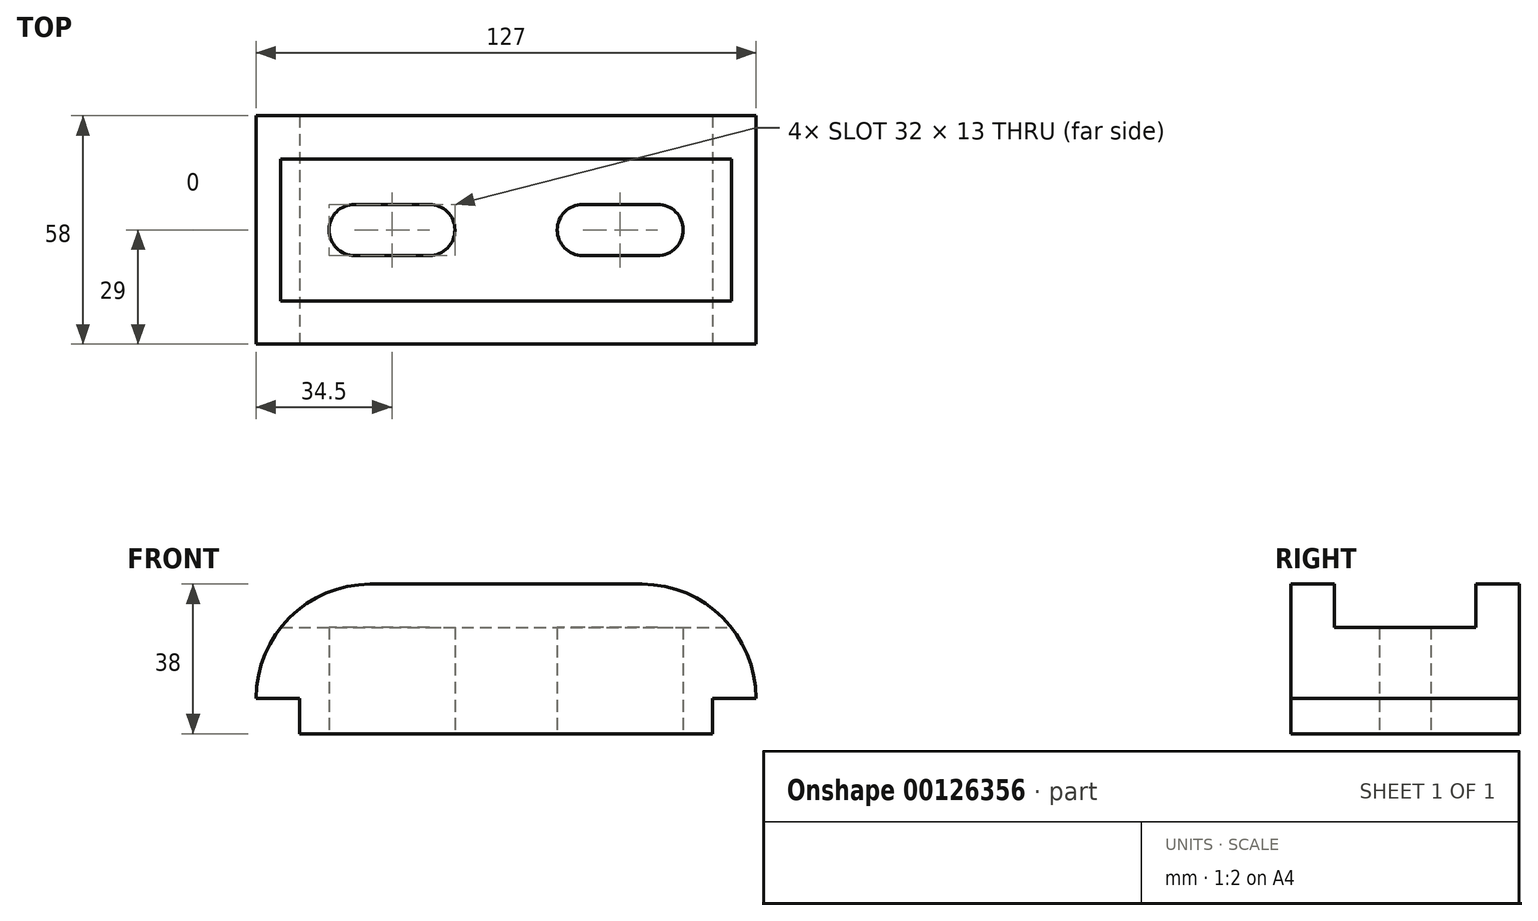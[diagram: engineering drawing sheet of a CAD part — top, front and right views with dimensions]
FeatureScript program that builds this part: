
annotation { "Feature Type Name" : "Feature", "Feature Type Description" : "" }
export const myFeature = defineFeature(function(context is Context, id is Id, definition is map)
    precondition{}
    {
        {
            var Q0;
            Q0=qCreatedBy(makeId("Front.planeOp"),FACE);
            var sketch = newSketch(context, id + "F0", { "sketchPlane" : qUnion([Q0])});
            skLineSegment(sketch, "E0", {"start": v(0, 0) * mm, "end": v(0, 9) * mm});
            skLineSegment(sketch, "E1", {"start": v(0, 9) * mm, "end": v(-11, 9) * mm});
            skLineSegment(sketch, "E2", {"start": v(-11, 9) * mm, "end": v(-11, 38) * mm});
            skLineSegment(sketch, "E3", {"start": v(0, 0) * mm, "end": v(105, 0) * mm});
            skLineSegment(sketch, "E4", {"start": v(105, 0) * mm, "end": v(105, 9) * mm});
            skLineSegment(sketch, "E5", {"start": v(105, 9) * mm, "end": v(116, 9) * mm});
            skLineSegment(sketch, "E6", {"start": v(116, 9) * mm, "end": v(116, 38) * mm});
            skLineSegment(sketch, "E7", {"start": v(116, 38) * mm, "end": v(-11, 38) * mm});
            skArc(sketch, "E8", {"start": v(18, 38) * mm, "mid": v(-2.5, 29.5) * mm, "end": v(-11, 9) * mm});
            skArc(sketch, "E9", {"start": v(116, 9) * mm, "mid": v(107.5, 29.5) * mm, "end": v(87, 38) * mm});
            skSolve(sketch);
        }
        {
            var Q0;
            Q0=makeQuery(id+"F0.imprint","IMPRINT",FACE,{"disambiguationData":[TD([[makeQuery(id+"F0.imprint","IMPRINT",EDGE,{"derivedFrom":sQuery(id+"F0.wireOp",EDGE,"E0")}),-1.0]])]});
            extrude(context, id + "F1", {"entities" : qUnion([Q0]), "oppositeDirection" : true, "depth" : 58 * mm});
        }
        {
            var Q0;
            Q0=qCreatedBy(makeId("Right.planeOp"),FACE);
            var sketch = newSketch(context, id + "F2", { "sketchPlane" : qUnion([Q0])});
            skLineSegment(sketch, "E10", {"start": v(0, 0) * mm, "end": v(11, 0) * mm, "construction": true});
            skLineSegment(sketch, "E11", {"start": v(11, 0) * mm, "end": v(47, 0) * mm, "construction": true});
            skLineSegment(sketch, "E12", {"start": v(11, 0) * mm, "end": v(11, 27) * mm, "construction": true});
            skLineSegment(sketch, "E13", {"start": v(11, 27) * mm, "end": v(11, 38) * mm});
            skLineSegment(sketch, "E14", {"start": v(11, 38) * mm, "end": v(47, 38) * mm});
            skLineSegment(sketch, "E15", {"start": v(47, 38) * mm, "end": v(47, 27) * mm});
            skLineSegment(sketch, "E16", {"start": v(47, 27) * mm, "end": v(11, 27) * mm});
            skSolve(sketch);
        }
        {
            var Q0;
            Q0 = qSketchRegion(id + "F2", true);
            extrude(context, id + "F3", {"entities" : qUnion([Q0]), "operationType" : NewBodyOperationType.REMOVE, "endBound" : BoundingType.SYMMETRIC, "oppositeDirection" : true, "depth" : 300 * mm});
        }
        {
            var Q0;
            Q0=makeQuery(id+"F1.opExtrude","SWEPT_FACE",FACE,{"disambiguationData":[OSD([sQuery(id+"F0.wireOp",EDGE,"E3")])]});
            var sketch = newSketch(context, id + "F4", { "sketchPlane" : qUnion([Q0])});
            skLineSegment(sketch, "E17", {"start": v(0, 0) * mm, "end": v(0, -29) * mm, "construction": true});
            skLineSegment(sketch, "E18", {"start": v(0, -29) * mm, "end": v(14, -29) * mm, "construction": true});
            skLineSegment(sketch, "E19", {"start": v(14, -29) * mm, "end": v(33, -29) * mm, "construction": true});
            skLineSegment(sketch, "E20", {"start": v(105, -29) * mm, "end": v(91, -29) * mm, "construction": true});
            skPoint(sketch, "E20.endSnap0", {"position": v(105, -29) * mm});
            skLineSegment(sketch, "E21", {"start": v(91, -29) * mm, "end": v(72, -29) * mm, "construction": true});
            skArc(sketch, "E22", {"start": v(14, -22.5) * mm, "mid": v(7.5, -29) * mm, "end": v(14, -35.5) * mm});
            skArc(sketch, "E23", {"start": v(33, -35.5) * mm, "mid": v(39.5, -29) * mm, "end": v(33, -22.5) * mm});
            skArc(sketch, "E24", {"start": v(72, -22.5) * mm, "mid": v(65.5, -29) * mm, "end": v(72, -35.5) * mm});
            skArc(sketch, "E25", {"start": v(91, -35.5) * mm, "mid": v(97.5, -29) * mm, "end": v(91, -22.5) * mm});
            skLineSegment(sketch, "E26", {"start": v(14, -22.5) * mm, "end": v(33, -22.5) * mm});
            skLineSegment(sketch, "E27", {"start": v(14, -35.5) * mm, "end": v(33, -35.5) * mm});
            skLineSegment(sketch, "E28", {"start": v(72, -22.5) * mm, "end": v(91, -22.5) * mm});
            skLineSegment(sketch, "E29", {"start": v(72, -35.5) * mm, "end": v(91, -35.5) * mm});
            skSolve(sketch);
        }
        {
            var Q0;
            Q0=makeQuery(id+"F4.imprint","IMPRINT",FACE,{"disambiguationData":[TD([[makeQuery(id+"F4.imprint","IMPRINT",EDGE,{"derivedFrom":sQuery(id+"F4.wireOp",EDGE,"E24")}),1.0]])]});
            var Q1;
            Q1=makeQuery(id+"F4.imprint","IMPRINT",FACE,{"disambiguationData":[TD([[makeQuery(id+"F4.imprint","IMPRINT",EDGE,{"derivedFrom":sQuery(id+"F4.wireOp",EDGE,"E22")}),1.0]])]});
            var Q2;
            Q2=sQuery(id+"F4.wireOp",EDGE,"E23");
            var Q3;
            Q3=sQuery(id+"F4.wireOp",EDGE,"E26");
            var Q4;
            Q4=sQuery(id+"F4.wireOp",EDGE,"E25");
            var Q5;
            Q5=sQuery(id+"F4.wireOp",EDGE,"E29");
            var Q6;
            Q6=sQuery(id+"F4.wireOp",EDGE,"E28");
            var Q7;
            Q7=sQuery(id+"F4.wireOp",EDGE,"E27");
            var Q8;
            Q8=sQuery(id+"F4.wireOp",EDGE,"E22");
            var Q9;
            Q9=sQuery(id+"F4.wireOp",EDGE,"E24");
            extrude(context, id + "F5", {"entities" : qUnion([Q0, Q1]), "operationType" : NewBodyOperationType.REMOVE, "surfaceEntities" : qUnion([Q2, Q3, Q4, Q5, Q6, Q7, Q8, Q9]), "oppositeDirection" : true, "depth" : 60 * mm});
        }
    });
